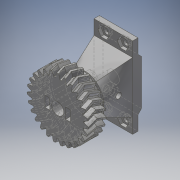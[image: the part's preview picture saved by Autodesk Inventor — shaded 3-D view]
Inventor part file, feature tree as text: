
AUTODESK INVENTOR PART (.ipt)
format: ipt  version: 2019 (Build 230136000, 136)  size: 1,003,520 bytes
history: native  units: mm (DEFAULTED — no unit token found)
features: sketch x23, extrude x15, plane x9, hole x6, other x4, mirror x4, chamfer x4, loft x1
ambient origin geometry x8: Origin, YZ Plane, XZ Plane, XY Plane, X Axis, Y Axis, Z Axis, Center Point
bodies: Solid1 (feature_tree)
feature tree (66):
  extrude  "Extrusion1"  Depth=5.0mm TaperAngle=0.0deg
  plane  "Work Plane2"
  plane  "Work Plane8"
  plane  "Work Plane9"
  other  "Spur Gear"
  mirror  "Mirror1"
  plane  "Work Plane11"
  extrude  "Extrusion2"  Depth=10.0mm TaperAngle=0.0deg
  extrude  "Extrusion3"  Depth=1.163553mm TaperAngle=0.0deg
  chamfer  "Chamfer1"  [1 undecoded]
  hole  "Hole1"  [1 undecoded]
  hole  "Hole2"  [1 undecoded]
  extrude  "Extrusion4"  Depth=3.75mm TaperAngle=45.0deg
  plane  "Work Plane13"
  extrude  "Extrusion5"  Depth=10.0mm
  plane  "Work Plane14"
  hole  "Hole3"  [1 undecoded]
  plane  "Work Plane15"
  hole  "Hole4"  [1 undecoded]
  extrude  "Extrusion6"  Depth=10.0mm
  extrude  "Extrusion7"  [1 undecoded]
  chamfer  "Chamfer2"  Distance=8.0mm
  extrude  "Extrusion9"  Depth=0.75mm TaperAngle=45.0deg
  extrude  "Extrusion10"  Depth=45.1mm
  chamfer  "Chamfer4"  Distance=5.0mm
  extrude  "Extrusion11"  Depth=10.0mm
  hole  "Hole5"  [1 undecoded]
  extrude  "Extrusion12"  Depth=10.0mm TaperAngle=0.0deg
  mirror  "Mirror2"
  plane  "Work Plane16"
  extrude  "Extrusion13"  Depth=10.0mm
  mirror  "Mirror3"
  chamfer  "Chamfer6"  Distance=5.5mm
  extrude  "Extrusion14"  Depth=10.0mm TaperAngle=0.0deg
  loft  "Loft1"
  extrude  "Extrusion15"  Depth=10.0mm TaperAngle=0.0deg
  plane  "Work Plane17"
  extrude  "Extrusion16"  Depth=10.0mm TaperAngle=45.0deg
  hole  "Hole6"  [1 undecoded]
  mirror  "Mirror4"
  sketch  "Sketch1"  dims[d0=34.130032mm d1=5.0mm d2=0.0mm]
  sketch  "Sketch2"  dims[d3=31.880377mm d4=10.0mm d5=0.0mm]
  other  "Srf1"
  sketch  "Sketch6"  dims[d16=31.29mm d17=0.0mm d34=1.163553mm]
  sketch  "Sketch7"  dims[d39=0.0mm]
  sketch  "Sketch9"  dims[d41=0.0mm]
  sketch  "Sketch10"  dims[d43=31.29mm]
  sketch  "Sketch11"  dims[d46=31.29mm d47=0.0mm d48=0.0mm]
  sketch  "Sketch12"  dims[d49=5.0mm d52=29.0mm]
  sketch  "Sketch13"  dims[d53=20.0mm d54=0.0mm d55=20.0mm]
  sketch  "Sketch14"  dims[d56=15.0mm d57=0.0mm d58=3.75mm d59=2.0mm d60=45.0deg]
  sketch  "Sketch15"  dims[d61=7.5mm d62=6.0mm d63=4.0mm d64=2.0mm d65=90.0deg d66=8.0mm d67=20.594885mm]
  sketch  "Sketch16"  dims[d68=6.5mm d69=6.0mm d70=4.0mm d71=2.0mm d72=90.0deg d73=8.0mm d74=0.0mm d75=10.0mm]
  sketch  "Sketch18"  dims[d76=1.0mm d77=10.0mm d78=0.0mm]
  sketch  "Sketch19"  dims[d79=10.0mm d80=1.0mm]
  sketch  "Sketch20"  dims[d81=20.0mm d82=0.0mm d83=10.0mm]
  sketch  "Sketch21"  dims[d84=3.5mm]
  sketch  "Sketch22"  dims[d85=3.5mm d86=6.0mm d87=6.0mm d88=7.0mm d89=90.0deg d90=8.0mm d91=0.0mm d92=-10.0mm]
  sketch  "Sketch23"  dims[d93=3.5mm d94=6.0mm d95=4.0mm d96=5.0mm d97=90.0deg d98=8.0mm d99=0.0mm]
  sketch  "Sketch24"  dims[d100=5.5mm d101=8.0mm d102=0.0mm]
  sketch  "Sketch26"  dims[d103=1.0mm d104=0.0mm d110=0.75mm d111=2.0mm d112=45.0deg]
  other  "Edges1"
  sketch  "Sketch27"  dims[d116=21.5mm d117=45.1mm d118=5.0mm d119=0.0mm]
  sketch  "Sketch28"  dims[d120=10.0mm d121=10.0mm]
  sketch  "Sketch29"  dims[d122=2.0mm d123=0.0mm d124=2.0mm d125=2.0mm d126=45.0deg d127=2.0mm d128=0.0mm d132=3.5mm d133=6.0mm d134=4.0mm d135=5.0mm d136=90.0deg d137=8.0mm d138=0.0mm d139=5.5mm d140=5.5mm d141=1.75mm d142=0.0mm d143=10.0mm d144=1.75mm d145=0.0mm d146=4.5mm d147=2.0mm d148=45.0deg d149=10.0mm d150=0.0mm d151=21.5mm d152=0.0mm d153=90.0deg d154=0.0mm d155=90.0deg d156=6.7mm d157=31.0mm d158=0.0mm d159=-5.0mm d160=5.9mm d161=2.7mm d162=0.0mm d163=3.1mm d164=6.0mm d165=6.5mm d166=7.5mm d167=90.0deg d168=10.0mm d169=0.0mm]
  other  "Pitch Diameter"
note: 8 required parameter values undecoded (feature->parameter linkage not recoverable at this tier; creation-order binding heuristic only, values carry confidence <= 0.55)
